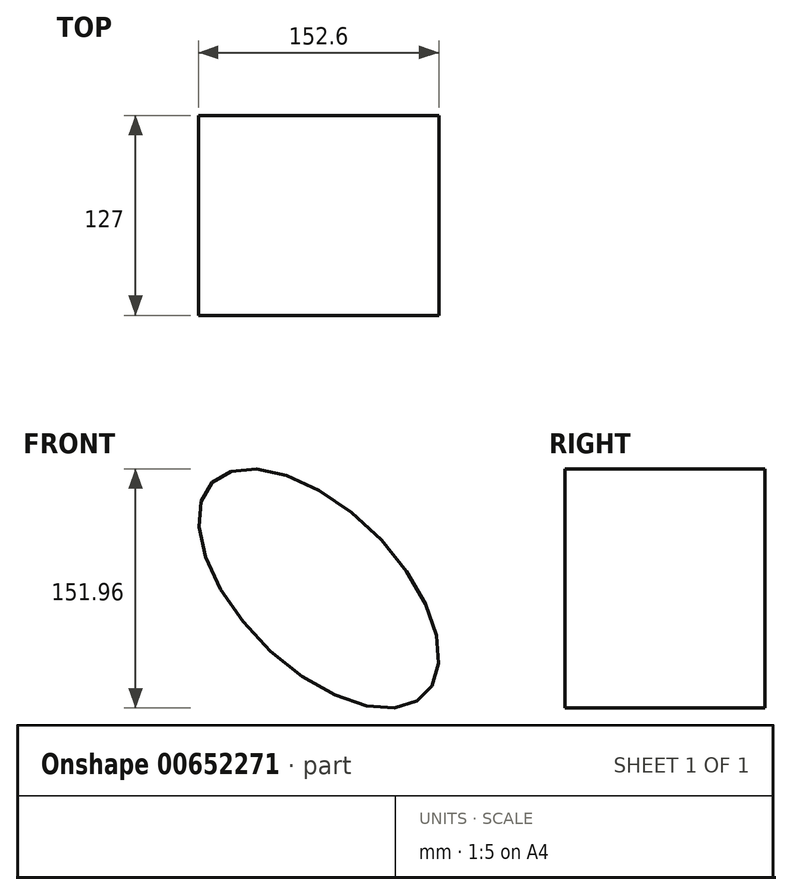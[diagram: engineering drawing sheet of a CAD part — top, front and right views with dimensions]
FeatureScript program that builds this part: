
annotation { "Feature Type Name" : "Feature", "Feature Type Description" : "" }
export const myFeature = defineFeature(function(context is Context, id is Id, definition is map)
    precondition{}
    {
        {
            var Q0;
            Q0=qCreatedBy(makeId("Front.planeOp"),FACE);
            var sketch = newSketch(context, id + "F0", { "sketchPlane" : qUnion([Q0])});
            skEllipse(sketch, "E0", {"center": v(0, 0) * mm, "majorRadius": 95.39 * mm, "minorRadius": 49.95 * mm, "majorAxis": v(-0.7, 0.7)});
            skSolve(sketch);
        }
        {
            var Q0;
            Q0 = qSketchRegion(id + "F0", true);
            extrude(context, id + "F1", {"entities" : qUnion([Q0]), "depth" : 127 * mm, "offsetDistance" : 25.4 * mm});
        }
    });
